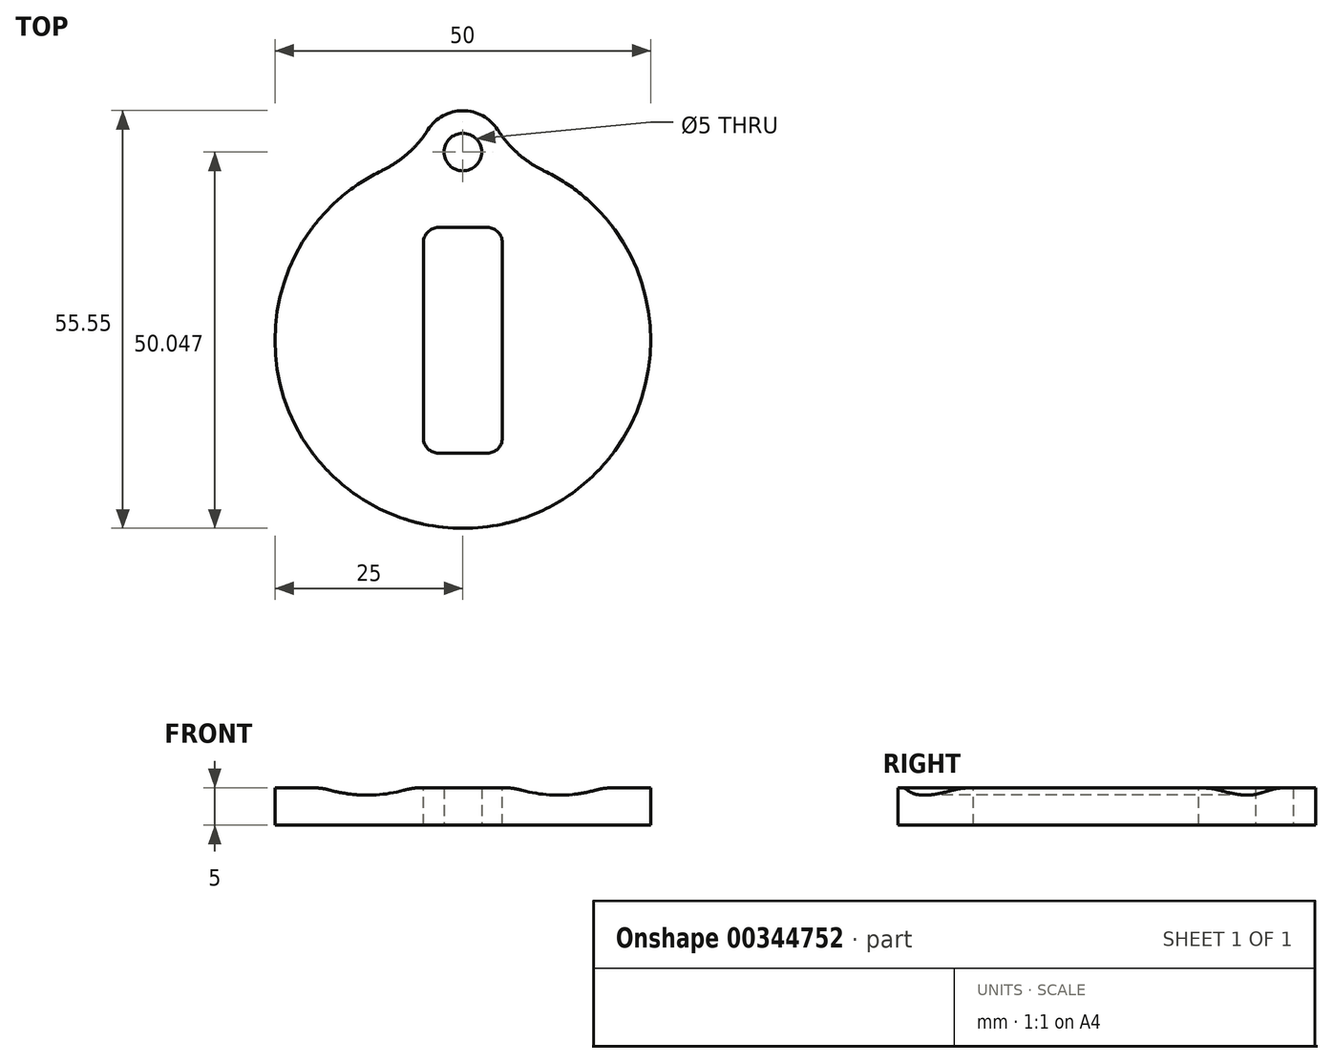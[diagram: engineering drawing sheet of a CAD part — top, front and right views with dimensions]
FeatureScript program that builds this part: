
annotation { "Feature Type Name" : "Feature", "Feature Type Description" : "" }
export const myFeature = defineFeature(function(context is Context, id is Id, definition is map)
    precondition{}
    {
        {
            var Q0;
            Q0=qCreatedBy(makeId("Top.planeOp"),FACE);
            var sketch = newSketch(context, id + "F0", { "sketchPlane" : qUnion([Q0])});
            skArc(sketch, "E0", {"start": v(-10.8, 22.55) * mm, "mid": v(0, -25) * mm, "end": v(10.8, 22.55) * mm});
            skCircle(sketch, "E1", {"center": v(0, 25.05) * mm, "radius": 2.5 * mm});
            skArc(sketch, "E2", {"start": v(4.64, 28) * mm, "mid": v(0, 30.55) * mm, "end": v(-4.64, 28) * mm});
            skArc(sketch, "E3", {"start": v(-10.8, 22.55) * mm, "mid": v(-7.34, 24.84) * mm, "end": v(-4.64, 28) * mm});
            skArc(sketch, "E4", {"start": v(4.64, 28) * mm, "mid": v(7.34, 24.84) * mm, "end": v(10.8, 22.55) * mm});
            skLineSegment(sketch, "E5", {"start": v(-10.8, 22.55) * mm, "end": v(10.8, 22.55) * mm, "construction": true});
            skSolve(sketch);
        }
        {
            var Q0;
            Q0=makeQuery(id+"F0.imprint","IMPRINT",FACE,{"disambiguationData":[TD([[makeQuery(id+"F0.imprint","IMPRINT",EDGE,{"derivedFrom":sQuery(id+"F0.wireOp",EDGE,"E0")}),1.0]])]});
            extrude(context, id + "F1", {"entities" : qUnion([Q0]), "endBound" : BoundingType.SYMMETRIC, "depth" : 5 * mm});
        }
        {
            var Q0;
            Q0=makeQuery(id+"F1.opExtrude","CAP_FACE",FACE,{"disambiguationData":[OSD([sQuery(id+"F0.wireOp",EDGE,"E0"),sQuery(id+"F0.wireOp",EDGE,"E1"),sQuery(id+"F0.wireOp",EDGE,"E2"),sQuery(id+"F0.wireOp",EDGE,"E3"),sQuery(id+"F0.wireOp",EDGE,"E4")])],"isStart":false});
            var sketch = newSketch(context, id + "F2", { "sketchPlane" : qUnion([Q0])});
            skLineSegment(sketch, "E6.bottom", {"start": v(5.25, 15) * mm, "end": v(-5.25, 15) * mm});
            skLineSegment(sketch, "E6.top", {"start": v(5.25, -15) * mm, "end": v(-5.25, -15) * mm});
            skLineSegment(sketch, "E6.left", {"start": v(5.25, 15) * mm, "end": v(5.25, -15) * mm});
            skLineSegment(sketch, "E6.right", {"start": v(-5.25, 15) * mm, "end": v(-5.25, -15) * mm});
            skPoint(sketch, "E6.middle", {"position": v(0, 0) * mm});
            skSolve(sketch);
        }
        {
            var Q0;
            Q0=makeQuery(id+"F2.imprint","IMPRINT",FACE,{"disambiguationData":[TD([[makeQuery(id+"F2.imprint","IMPRINT",EDGE,{"derivedFrom":sQuery(id+"F2.wireOp",EDGE,"E6.bottom")}),1.0]])]});
            extrude(context, id + "F3", {"entities" : qUnion([Q0]), "operationType" : NewBodyOperationType.REMOVE, "endBound" : BoundingType.THROUGH_ALL, "oppositeDirection" : true, "depth" : 25 * mm});
        }
        {
            var Q0;
            Q0=qCreatedBy(makeId("Front.planeOp"),FACE);
            var sketch = newSketch(context, id + "F4", { "sketchPlane" : qUnion([Q0])});
            skArc(sketch, "E7", {"start": v(0, 33.42) * mm, "mid": v(-31.23, 20) * mm, "end": v(0, 6.58) * mm});
            skLineSegment(sketch, "E8", {"start": v(-18.73, 2.5) * mm, "end": v(-6.73, 2.5) * mm, "construction": true});
            skLineSegment(sketch, "E9", {"start": v(-29.1, 0) * mm, "end": v(29.53, 0) * mm, "construction": true});
            skLineSegment(sketch, "E10", {"start": v(-26.6, 1.5) * mm, "end": v(30.63, 1.5) * mm, "construction": true});
            skCircle(sketch, "E11", {"center": v(-5.25, -7.5) * mm, "radius": 10 * mm, "construction": true});
            skLineSegment(sketch, "E12", {"start": v(0, -0.66) * mm, "end": v(0, 3.92) * mm, "construction": true});
            skArc(sketch, "E13.MirrorC", {"start": v(0, 33.42) * mm, "mid": v(31.23, 20) * mm, "end": v(0, 6.58) * mm});
            skArc(sketch, "E14.MirrorCS", {"start": v(0, -33.42) * mm, "mid": v(-31.23, -20) * mm, "end": v(0, -6.58) * mm, "construction": true});
            skArc(sketch, "E15.MirrorCS", {"start": v(0, -33.42) * mm, "mid": v(31.23, -20) * mm, "end": v(0, -6.58) * mm, "construction": true});
            skSolve(sketch);
        }
        {
            var Q0;
            Q0=makeQuery(id+"F4.imprint","IMPRINT",FACE,{"disambiguationData":[TD([[makeQuery(id+"F4.imprint","IMPRINT",EDGE,{"derivedFrom":sQuery(id+"F4.wireOp",EDGE,"E7")}),1.0]])]});
            extrude(context, id + "F5", {"entities" : qUnion([Q0]), "operationType" : NewBodyOperationType.REMOVE, "endBound" : BoundingType.THROUGH_ALL, "oppositeDirection" : true, "depth" : 25 * mm, "hasSecondDirection" : true, "secondDirectionBound" : SecondDirectionBoundingType.THROUGH_ALL, "secondDirectionOppositeDirection" : false, "secondDirectionDepth" : 25 * mm});
        }
        {
            var Q0;
            Q0=makeQuery(id+"F5.boolean.opBoolean","INTERSECT",EDGE,{"disambiguationData":[OD(0.0)],"derivedFrom":[makeQuery(id+"F1.opExtrude","CAP_FACE",FACE,{"disambiguationData":[OSD([sQuery(id+"F0.wireOp",EDGE,"E0"),sQuery(id+"F0.wireOp",EDGE,"E1"),sQuery(id+"F0.wireOp",EDGE,"E2"),sQuery(id+"F0.wireOp",EDGE,"E3"),sQuery(id+"F0.wireOp",EDGE,"E4")])],"isStart":false}),makeQuery(id+"F5.opExtrude","SWEPT_FACE",FACE,{"disambiguationData":[OSD([sQuery(id+"F4.wireOp",EDGE,"E7")])]})]});
            var Q1;
            Q1=makeQuery(id+"F5.boolean.opBoolean","INTERSECT",EDGE,{"disambiguationData":[OD(1.0)],"derivedFrom":[makeQuery(id+"F1.opExtrude","CAP_FACE",FACE,{"disambiguationData":[OSD([sQuery(id+"F0.wireOp",EDGE,"E0"),sQuery(id+"F0.wireOp",EDGE,"E1"),sQuery(id+"F0.wireOp",EDGE,"E2"),sQuery(id+"F0.wireOp",EDGE,"E3"),sQuery(id+"F0.wireOp",EDGE,"E4")])],"isStart":false}),makeQuery(id+"F5.opExtrude","SWEPT_FACE",FACE,{"disambiguationData":[OSD([sQuery(id+"F4.wireOp",EDGE,"E7")])]})]});
            var Q2;
            Q2=makeQuery(id+"F5.boolean.opBoolean","INTERSECT",EDGE,{"disambiguationData":[OD(1.0)],"derivedFrom":[makeQuery(id+"F1.opExtrude","CAP_FACE",FACE,{"disambiguationData":[OSD([sQuery(id+"F0.wireOp",EDGE,"E0"),sQuery(id+"F0.wireOp",EDGE,"E1"),sQuery(id+"F0.wireOp",EDGE,"E2"),sQuery(id+"F0.wireOp",EDGE,"E3"),sQuery(id+"F0.wireOp",EDGE,"E4")])],"isStart":false}),makeQuery(id+"F5.opExtrude","SWEPT_FACE",FACE,{"disambiguationData":[OSD([sQuery(id+"F4.wireOp",EDGE,"E13.MirrorC")])]})]});
            var Q3;
            Q3=makeQuery(id+"F5.boolean.opBoolean","INTERSECT",EDGE,{"disambiguationData":[OD(0.0)],"derivedFrom":[makeQuery(id+"F1.opExtrude","CAP_FACE",FACE,{"disambiguationData":[OSD([sQuery(id+"F0.wireOp",EDGE,"E0"),sQuery(id+"F0.wireOp",EDGE,"E1"),sQuery(id+"F0.wireOp",EDGE,"E2"),sQuery(id+"F0.wireOp",EDGE,"E3"),sQuery(id+"F0.wireOp",EDGE,"E4")])],"isStart":false}),makeQuery(id+"F5.opExtrude","SWEPT_FACE",FACE,{"disambiguationData":[OSD([sQuery(id+"F4.wireOp",EDGE,"E13.MirrorC")])]})]});
            fillet(context, id + "F6", {"entities" : qUnion([Q0, Q1, Q2, Q3]), "radius" : 10 * mm, "tangentPropagation" : true, "allowEdgeOverflow" : false});
        }
        {
            var Q0;
            Q0=makeQuery(id+"F3.boolean.opBoolean","COPY",EDGE,{"derivedFrom":makeQuery(id+"F3.opExtrude","SWEPT_EDGE",EDGE,{"disambiguationData":[OSD([sQuery(id+"F2.wireOp",EDGE,"E6.bottom"),sQuery(id+"F2.wireOp",EDGE,"E6.left")])]})});
            var Q1;
            Q1=makeQuery(id+"F3.boolean.opBoolean","COPY",EDGE,{"derivedFrom":makeQuery(id+"F3.opExtrude","SWEPT_EDGE",EDGE,{"disambiguationData":[OSD([sQuery(id+"F2.wireOp",EDGE,"E6.top"),sQuery(id+"F2.wireOp",EDGE,"E6.left")])]})});
            var Q2;
            Q2=makeQuery(id+"F3.boolean.opBoolean","COPY",EDGE,{"derivedFrom":makeQuery(id+"F3.opExtrude","SWEPT_EDGE",EDGE,{"disambiguationData":[OSD([sQuery(id+"F2.wireOp",EDGE,"E6.top"),sQuery(id+"F2.wireOp",EDGE,"E6.right")])]})});
            var Q3;
            Q3=makeQuery(id+"F3.boolean.opBoolean","COPY",EDGE,{"derivedFrom":makeQuery(id+"F3.opExtrude","SWEPT_EDGE",EDGE,{"disambiguationData":[OSD([sQuery(id+"F2.wireOp",EDGE,"E6.bottom"),sQuery(id+"F2.wireOp",EDGE,"E6.right")])]})});
            fillet(context, id + "F7", {"entities" : qUnion([Q0, Q1, Q2, Q3]), "radius" : 2 * mm, "tangentPropagation" : true, "allowEdgeOverflow" : false});
        }
    });
